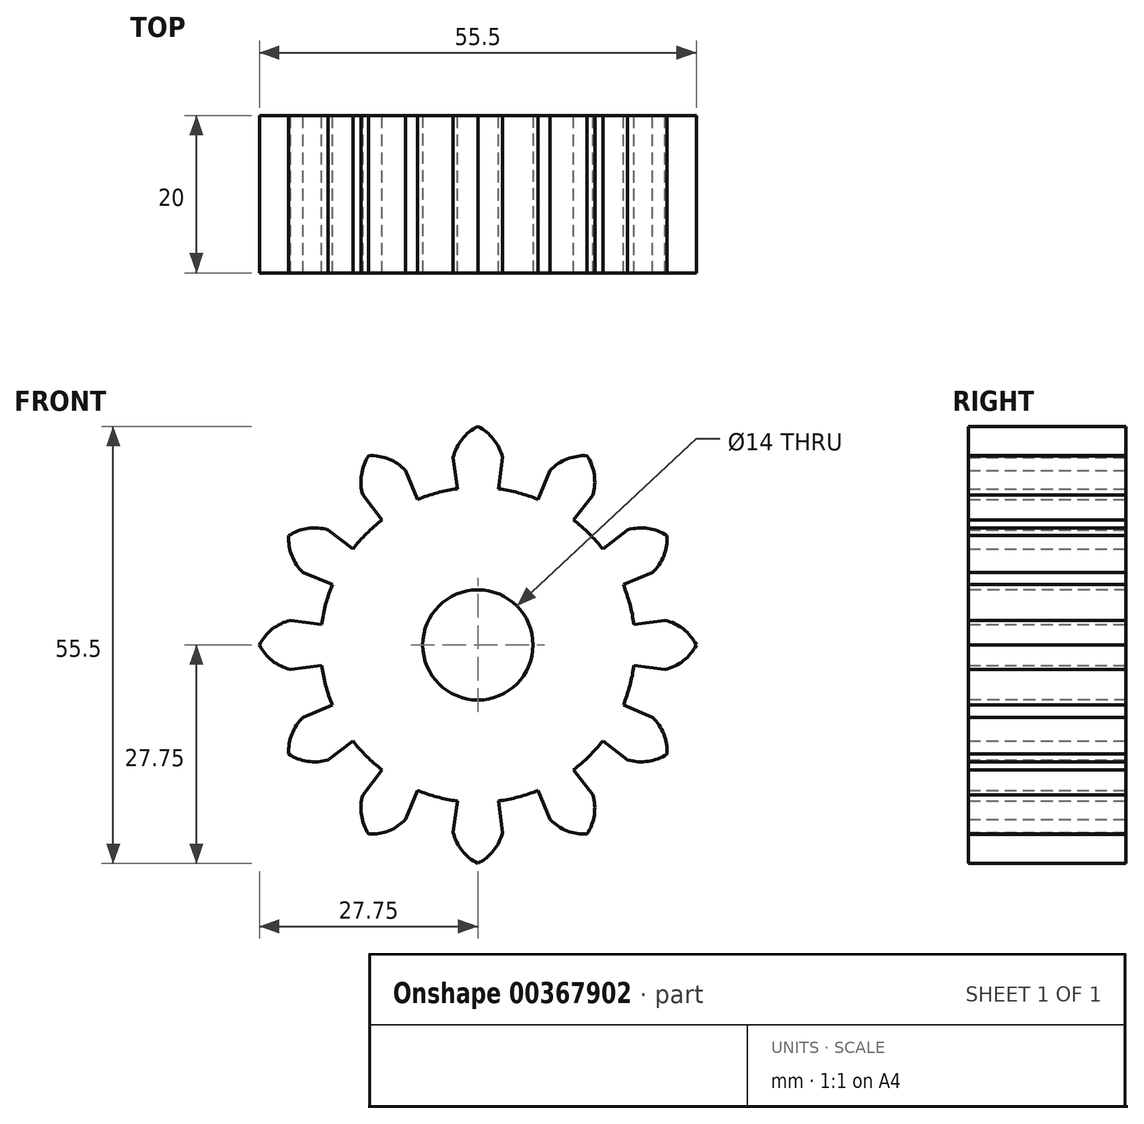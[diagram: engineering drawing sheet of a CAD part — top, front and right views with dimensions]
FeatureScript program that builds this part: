
annotation { "Feature Type Name" : "Feature", "Feature Type Description" : "" }
export const myFeature = defineFeature(function(context is Context, id is Id, definition is map)
    precondition{}
    {
        {
            assignVariable(context, id + "F0", {"name" : "N", "anyValue" : 12});
        }
        {
            var Q0;
            Q0=qCreatedBy(makeId("Front.planeOp"),FACE);
            var sketch = newSketch(context, id + "F1", { "sketchPlane" : qUnion([Q0])});
            skCircle(sketch, "E0", {"center": v(0, 0) * mm, "radius": 20 * mm});
            skCircle(sketch, "E1", {"center": v(0, 0) * mm, "radius": 24 * mm, "construction": true});
            skCircle(sketch, "E2", {"center": v(0, 0) * mm, "radius": 28 * mm, "construction": true});
            skLineSegment(sketch, "E3", {"start": v(3.13, 23.8) * mm, "end": v(-53.59, 31.26) * mm, "construction": true});
            skLineSegment(sketch, "E4", {"start": v(-55.6, 10.77) * mm, "end": v(3.13, 23.8) * mm, "construction": true});
            skCircle(sketch, "E5", {"center": v(0, 0) * mm, "radius": 22.55 * mm, "construction": true});
            skCircle(sketch, "E6", {"center": v(3.13, 23.8) * mm, "radius": 6 * mm, "construction": true});
            skCircle(sketch, "E7", {"center": v(-2.7, 22.4) * mm, "radius": 6 * mm, "construction": true});
            skLineSegment(sketch, "E8", {"start": v(0, 0) * mm, "end": v(-11.02, 83.68) * mm, "construction": true});
            skLineSegment(sketch, "E9", {"start": v(-11.02, 83.68) * mm, "end": v(11.02, 83.68) * mm, "construction": true});
            skLineSegment(sketch, "E10", {"start": v(11.02, 83.68) * mm, "end": v(0, 0) * mm, "construction": true});
            skLineSegment(sketch, "E11", {"start": v(0, 0) * mm, "end": v(0, 83.68) * mm, "construction": true});
            skLineSegment(sketch, "E12", {"start": v(2.61, 19.83) * mm, "end": v(3.13, 23.8) * mm});
            skArc(sketch, "E13", {"start": v(3.13, 23.8) * mm, "mid": v(1.8, 26.35) * mm, "end": v(-0.56, 28) * mm});
            skArc(sketch, "E14", {"start": v(-0.56, 28) * mm, "mid": v(0.28, -28) * mm, "end": v(0, 28) * mm});
            skLineSegment(sketch, "E15.MirrorCS", {"start": v(-2.61, 19.83) * mm, "end": v(-3.13, 23.8) * mm});
            skArc(sketch, "E16.MirrorCS", {"start": v(-3.13, 23.8) * mm, "mid": v(-1.8, 26.35) * mm, "end": v(0.56, 28) * mm});
            skArc(sketch, "E17.MirrorCS", {"start": v(0.56, 28) * mm, "mid": v(-0.28, -28) * mm, "end": v(0, 28) * mm});
            skSolve(sketch);
        }
        {
            var Q0;
            {var subQ0=sQuery(id+"F1.wireOp",EDGE,"E0");var subQ1=makeQuery(id+"F1.imprint","INTERSECT",VERTEX,{"derivedFrom":[subQ0,sQuery(id+"F1.wireOp",EDGE,"E12")]});Q0=makeQuery(id+"F1.imprint","IMPRINT",FACE,{"disambiguationData":[TD([[makeQuery(id+"F1.imprint","IMPRINT",EDGE,{"disambiguationData":[TD([[subQ1,-1.0]])],"derivedFrom":subQ0}),1.0]])]});}
            var Q1;
            {var subQ0=sQuery(id+"F1.wireOp",EDGE,"E12");Q1=makeQuery(id+"F1.imprint","IMPRINT",FACE,{"disambiguationData":[TD([[makeQuery(id+"F1.imprint","IMPRINT",EDGE,{"derivedFrom":subQ0}),1.0]])]});}
            extrude(context, id + "F2", {"entities" : qUnion([Q0, Q1]), "endBound" : BoundingType.SYMMETRIC, "depth" : 20 * mm});
        }
        {
            var Q0;
            Q0=makeQuery(id+"F2.opExtrude","SWEPT_FACE",FACE,{"disambiguationData":[OSD([sQuery(id+"F1.wireOp",EDGE,"E12")])]});
            var Q1;
            Q1=makeQuery(id+"F2.opExtrude","SWEPT_FACE",FACE,{"disambiguationData":[OSD([sQuery(id+"F1.wireOp",EDGE,"E13")])]});
            var Q2;
            Q2=makeQuery(id+"F2.opExtrude","SWEPT_FACE",FACE,{"disambiguationData":[OSD([sQuery(id+"F1.wireOp",EDGE,"E16.MirrorCS")])]});
            var Q3;
            Q3=makeQuery(id+"F2.opExtrude","SWEPT_FACE",FACE,{"disambiguationData":[OSD([sQuery(id+"F1.wireOp",EDGE,"E15.MirrorCS")])]});
            var Q4;
            Q4=makeQuery(id+"F2.opExtrude","SWEPT_FACE",FACE,{"disambiguationData":[OSD([sQuery(id+"F1.wireOp",EDGE,"E0")])]});
            circularPattern(context, id + "F3", {"patternType" : PatternType.FACE, "faces" : qUnion([Q0, Q1, Q2, Q3]), "axis" : qUnion([Q4]), "angle" : 360 * degree, "instanceCount" : getVariable(context, 'N'), "equalSpace" : true});
        }
        {
            var Q0;
            Q0=makeQuery(id+"F2.opExtrude","CAP_FACE",FACE,{"disambiguationData":[OSD([sQuery(id+"F1.wireOp",EDGE,"E0"),sQuery(id+"F1.wireOp",EDGE,"E12"),sQuery(id+"F1.wireOp",EDGE,"E13"),sQuery(id+"F1.wireOp",EDGE,"E15.MirrorCS"),sQuery(id+"F1.wireOp",EDGE,"E16.MirrorCS")])],"isStart":false});
            var sketch = newSketch(context, id + "F4", { "sketchPlane" : qUnion([Q0])});
            skCircle(sketch, "E18", {"center": v(0, 0) * mm, "radius": 7 * mm});
            skSolve(sketch);
        }
        {
            var Q0;
            Q0=makeQuery(id+"F4.imprint","IMPRINT",FACE,{"disambiguationData":[TD([[makeQuery(id+"F4.imprint","IMPRINT",EDGE,{"derivedFrom":sQuery(id+"F4.wireOp",EDGE,"E18")}),1.0]])]});
            extrude(context, id + "F5", {"entities" : qUnion([Q0]), "operationType" : NewBodyOperationType.REMOVE, "endBound" : BoundingType.THROUGH_ALL, "oppositeDirection" : true, "depth" : 25 * mm});
        }
    });
